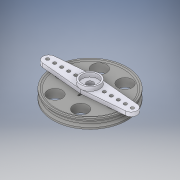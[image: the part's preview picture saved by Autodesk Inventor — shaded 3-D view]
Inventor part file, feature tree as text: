
AUTODESK INVENTOR PART (.ipt)
format: ipt  version: 2019 (Build 230136000, 136)  size: 399,360 bytes
history: native  units: in
note: dims shown in document units (in); Inventor stores cm internally (conversion verified against a paired STEP export)
features: extrude x11, sketch x11, fillet x3, plane x1, projected_geometry x1
ambient origin geometry x8: Origin, YZ Plane, XZ Plane, XY Plane, X Axis, Y Axis, Z Axis, Center Point
bodies: Solid1 (feature_tree)
feature tree (27):
  extrude  "Extrusion1"  Depth=0.1772in
  plane  "Work Plane1"
  extrude  "Extrusion2"  Depth=0.1181in TaperAngle=360.0deg
  fillet  "Fillet1"  Radius=0.1181in
  extrude  "Extrusion3"  Depth=0.8661in
  extrude  "Extrusion8"  Depth=0.2362in
  extrude  "Extrusion4"  Depth=0.0711in
  extrude  "Extrusion9"  Depth=0.0711in
  extrude  "Extrusion5"  Depth=0.2362in
  extrude  "Extrusion6"  Depth=0.0492in
  extrude  "Extrusion7"  Depth=0.0197in
  fillet  "Fillet2"  Radius=0.0197in
  extrude  "Extrusion10"  Depth=0.0197in
  extrude  "Extrusion11"  Depth=0.0689in
  fillet  "Fillet3"  Radius=0.0886in
  sketch  "Sketch1"  dims[d0=0.9055in d1=0.1772in]
  sketch  "Sketch2"  dims[d2=0.315in d3=2.3622in d5=360.0deg d7=0.1181in d8=0.0in]
  sketch  "Sketch3"  dims[d9=0.0787in d10=0.0in d11=0.8661in]
  sketch  "Sketch4"  dims[d12=0.0276in d13=0.2362in]
  sketch  "Sketch5"  dims[d14=0.1442in d15=0.0711in]
  sketch  "Sketch6"  dims[d16=1.0103in d17=0.0711in]
  sketch  "Sketch7"  dims[d18=0.2362in d19=0.1176in]
  projected_geometry  "Projected Loop1"
  sketch  "Sketch8"  dims[d20=0.0492in d21=0.0in d22=0.1969in]
  sketch  "Sketch9"  dims[d23=0.0492in d24=0.0in d25=0.1969in d26=0.0197in d27=0.0in]
  sketch  "Sketch10"  dims[d28=0.1378in d29=0.0197in]
  sketch  "Sketch11"  dims[d34=0.0689in d35=0.0689in d37=0.0886in d38=0.1772in d39=0.1772in d40=0.2756in d41=0.0197in d42=0.1721in d43=0.1168in d44=0.0702in d45=0.0703in d46=0.0673in d47=0.1881in d48=0.5231in d49=0.0886in d50=0.1378in d51=0.0in d52=0.4591in d53=0.0574in d54=0.1435in d55=0.3157in d56=0.4018in d57=0.2296in d58=0.0394in d59=0.0394in d60=0.0394in d61=0.0394in d62=0.0394in d63=0.0492in d64=0.0in d65=0.8661in d66=0.0079in d67=0.0in d68=0.8661in d69=0.0079in d70=0.0in d71=0.0098in d72=0.0in d73=0.0276in d74=0.0788in d75=0.1102in d76=0.0in d77=0.0039in d78=0.0in d79=0.1575in d80=0.1575in d81=0.0079in d82=0.0in d83=0.0276in]
